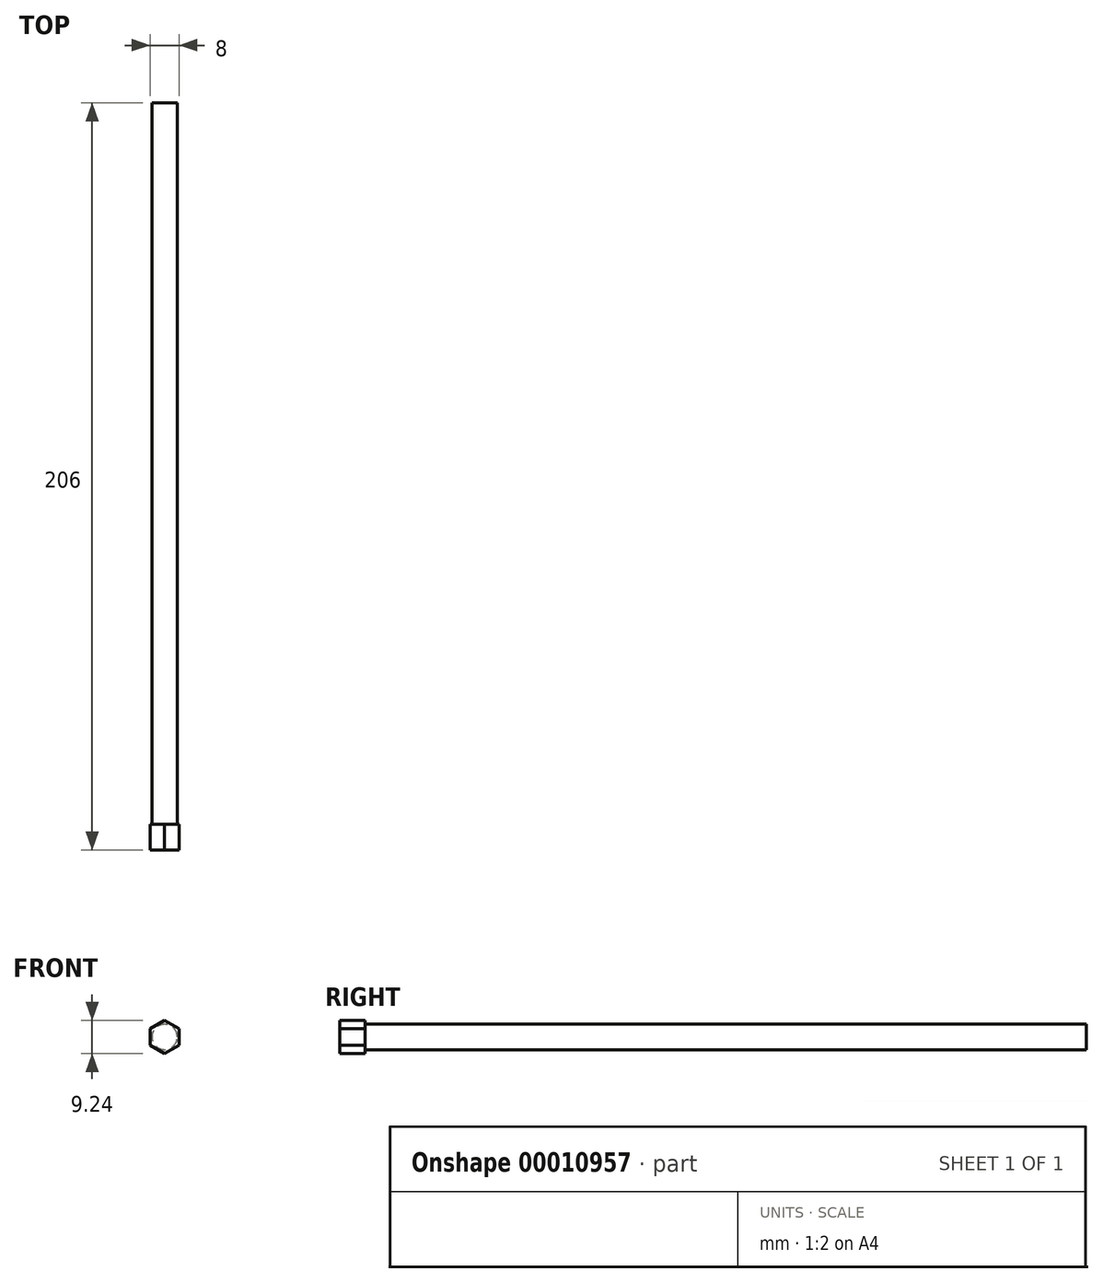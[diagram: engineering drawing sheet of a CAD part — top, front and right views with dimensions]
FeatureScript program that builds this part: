
annotation { "Feature Type Name" : "Feature", "Feature Type Description" : "" }
export const myFeature = defineFeature(function(context is Context, id is Id, definition is map)
    precondition{}
    {
        {
            var Q0;
            Q0=qCreatedBy(makeId("Front.planeOp"),FACE);
            var sketch = newSketch(context, id + "F0", { "sketchPlane" : qUnion([Q0])});
            skCircle(sketch, "E0", {"center": v(0, 0) * mm, "radius": 3.5 * mm});
            skSolve(sketch);
        }
        {
            var Q0;
            Q0=makeQuery(id+"F0.imprint","IMPRINT",FACE,{"disambiguationData":[TD([[makeQuery(id+"F0.imprint","IMPRINT",EDGE,{"derivedFrom":sQuery(id+"F0.wireOp",EDGE,"E0")}),1.0]])]});
            extrude(context, id + "F1", {"entities" : qUnion([Q0]), "depth" : 200 * mm});
        }
        {
            var Q0;
            Q0=makeQuery(id+"F1.opExtrude","CAP_FACE",FACE,{"disambiguationData":[OSD([sQuery(id+"F0.wireOp",EDGE,"E0")])],"isStart":false});
            var sketch = newSketch(context, id + "F2", { "sketchPlane" : qUnion([Q0])});
            skCircle(sketch, "E1.cCircle", {"center": v(0, 0) * mm, "radius": 4 * mm, "construction": true});
            skLineSegment(sketch, "E1.0", {"start": v(4, 2.3) * mm, "end": v(4, -2.3) * mm});
            skLineSegment(sketch, "E1.1", {"start": v(4, -2.3) * mm, "end": v(0, -4.62) * mm});
            skLineSegment(sketch, "E1.2", {"start": v(0, -4.62) * mm, "end": v(-4, -2.3) * mm});
            skLineSegment(sketch, "E1.3", {"start": v(-4, -2.3) * mm, "end": v(-4, 2.3) * mm});
            skLineSegment(sketch, "E1.4", {"start": v(-4, 2.3) * mm, "end": v(0, 4.62) * mm});
            skLineSegment(sketch, "E1.5", {"start": v(0, 4.62) * mm, "end": v(4, 2.3) * mm});
            skPoint(sketch, "E1.0.midPoint", {"position": v(4, 0) * mm});
            skSolve(sketch);
        }
        {
            var Q0;
            Q0=makeQuery(id+"F2.imprint","IMPRINT",FACE,{"disambiguationData":[TD([[makeQuery(id+"F2.imprint","IMPRINT",EDGE,{"derivedFrom":sQuery(id+"F2.wireOp",EDGE,"E1.0")}),-1.0]])]});
            var Q1;
            Q1=makeQuery(id+"F2.imprint","IMPRINT",FACE,{"disambiguationData":[TD([[makeQuery(id+"F2.imprint","IMPRINT",EDGE,{"derivedFrom":makeQuery(id+"F1.opExtrude","CAP_EDGE",EDGE,{"disambiguationData":[OSD([sQuery(id+"F0.wireOp",EDGE,"E0")])],"isStart":false})}),1.0]])]});
            extrude(context, id + "F3", {"entities" : qUnion([Q0, Q1]), "operationType" : NewBodyOperationType.ADD, "depth" : 6 * mm, "hasSecondDirection" : true, "secondDirectionOppositeDirection" : true, "secondDirectionDepth" : 1 * mm});
        }
    });
